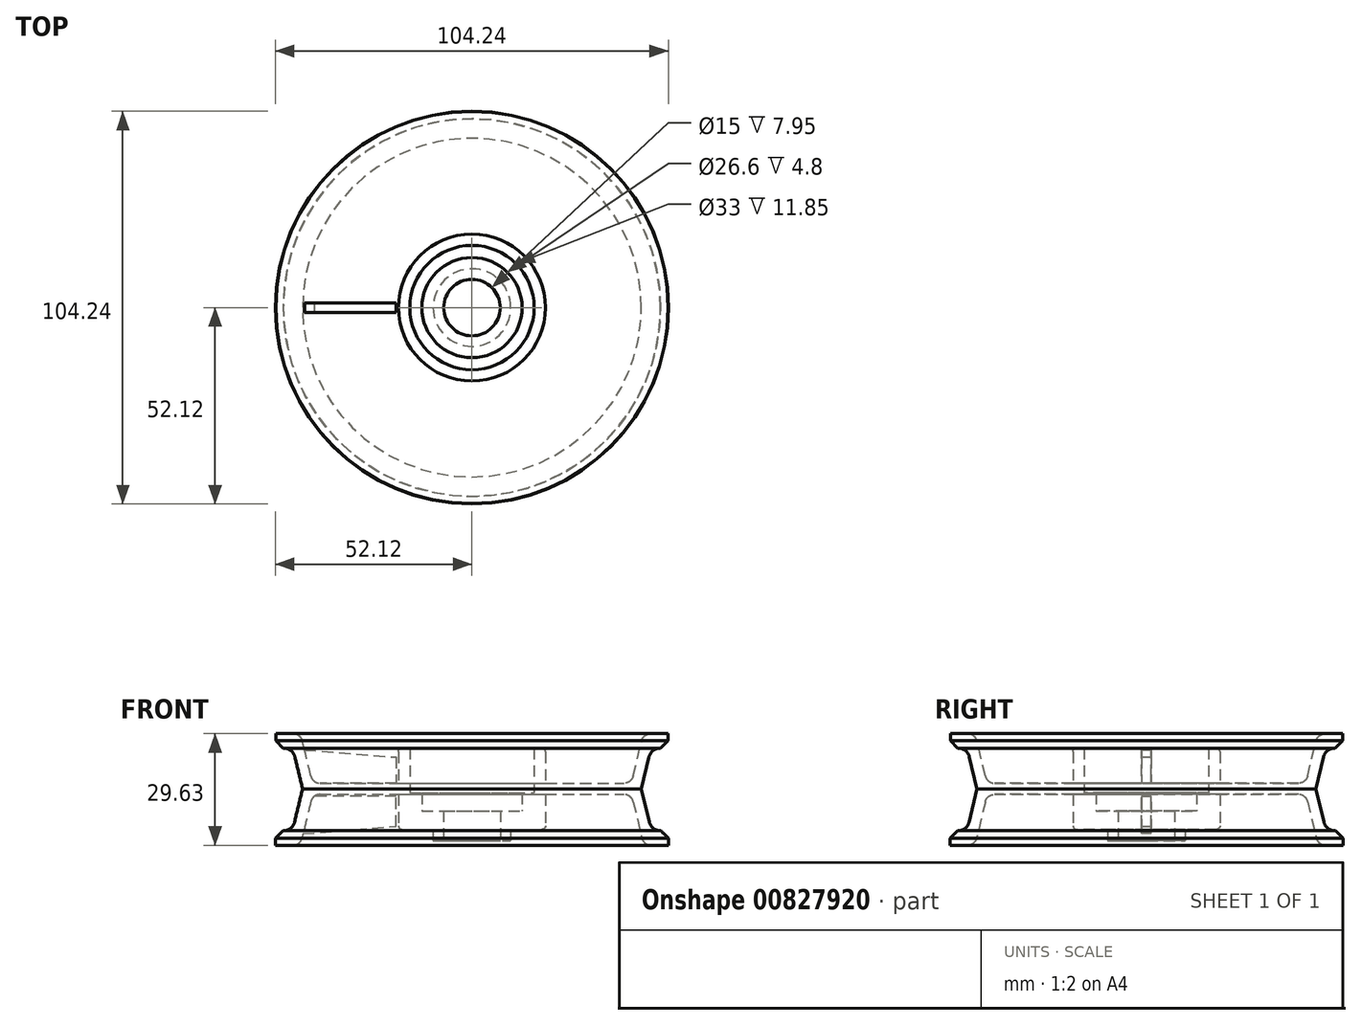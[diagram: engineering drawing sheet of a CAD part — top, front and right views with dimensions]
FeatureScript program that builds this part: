
annotation { "Feature Type Name" : "Feature", "Feature Type Description" : "" }
export const myFeature = defineFeature(function(context is Context, id is Id, definition is map)
    precondition{}
    {
        {
            var Q0;
            Q0=qCreatedBy(makeId("Front.planeOp"),FACE);
            var sketch = newSketch(context, id + "F0", { "sketchPlane" : qUnion([Q0])});
            skLineSegment(sketch, "E0", {"start": v(0, 0) * mm, "end": v(-7.5, 0) * mm, "construction": true});
            skLineSegment(sketch, "E1", {"start": v(-7.5, 0) * mm, "end": v(-10.3, 0) * mm});
            skLineSegment(sketch, "E2.bottom", {"start": v(-10.3, 0) * mm, "end": v(-7.5, 0) * mm});
            skLineSegment(sketch, "E2.top", {"start": v(-10.3, 0) * mm, "end": v(-7.5, 0) * mm});
            skLineSegment(sketch, "E2.left", {"start": v(-10.3, 0) * mm, "end": v(-10.3, 0) * mm});
            skLineSegment(sketch, "E2.right", {"start": v(-7.5, 0) * mm, "end": v(-7.5, 0) * mm});
            skLineSegment(sketch, "E3", {"start": v(-10.3, 0) * mm, "end": v(-10.3, 3) * mm});
            skLineSegment(sketch, "E4", {"start": v(-7.5, 0) * mm, "end": v(-7.5, 7.95) * mm});
            skLineSegment(sketch, "E5", {"start": v(-10.3, 3) * mm, "end": v(-19.5, 3) * mm});
            skLineSegment(sketch, "E6", {"start": v(-7.5, 7.95) * mm, "end": v(-13.3, 7.95) * mm});
            skLineSegment(sketch, "E7", {"start": v(-13.3, 7.95) * mm, "end": v(-13.3, 12.75) * mm});
            skLineSegment(sketch, "E8", {"start": v(-19.5, 3) * mm, "end": v(-19.5, 24.6) * mm});
            skLineSegment(sketch, "E9", {"start": v(-19.5, 24.6) * mm, "end": v(-16.5, 24.6) * mm});
            skLineSegment(sketch, "E10", {"start": v(-16.5, 24.6) * mm, "end": v(-16.5, 12.75) * mm});
            skLineSegment(sketch, "E11", {"start": v(-16.5, 12.75) * mm, "end": v(-13.3, 12.75) * mm});
            skPoint(sketch, "E12", {"position": v(-19.5, 13.8) * mm});
            skLineSegment(sketch, "E13.bottom", {"start": v(-19.5, 15.3) * mm, "end": v(-42.3, 15.3) * mm});
            skLineSegment(sketch, "E13.top", {"start": v(-19.5, 12.3) * mm, "end": v(-42.3, 12.3) * mm});
            skLineSegment(sketch, "E13.left", {"start": v(-19.5, 15.3) * mm, "end": v(-19.5, 12.3) * mm});
            skLineSegment(sketch, "E13.right", {"start": v(-42.3, 15.3) * mm, "end": v(-42.3, 12.3) * mm, "construction": true});
            skLineSegment(sketch, "E14", {"start": v(-42.3, 15.3) * mm, "end": v(-41.94, 13.8) * mm});
            skLineSegment(sketch, "E15", {"start": v(-42.3, 12.3) * mm, "end": v(-41.94, 13.8) * mm});
            skPoint(sketch, "E16", {"position": v(-42.3, 13.8) * mm});
            skPoint(sketch, "E17", {"position": v(-41.94, 13.8) * mm});
            skLineSegment(sketch, "E18", {"start": v(-42.3, 12.3) * mm, "end": v(-45.54, -1.2) * mm});
            skLineSegment(sketch, "E19", {"start": v(-42.3, 15.3) * mm, "end": v(-45.45, 28.43) * mm});
            skLineSegment(sketch, "E20", {"start": v(-41.94, 13.8) * mm, "end": v(-44.94, 13.8) * mm, "construction": true});
            skLineSegment(sketch, "E21", {"start": v(-44.94, 13.8) * mm, "end": v(-48.45, 28.43) * mm});
            skLineSegment(sketch, "E22", {"start": v(-48.45, 28.43) * mm, "end": v(-45.45, 28.43) * mm});
            skLineSegment(sketch, "E23", {"start": v(-44.94, 13.8) * mm, "end": v(-48.54, -1.2) * mm});
            skLineSegment(sketch, "E24", {"start": v(-48.54, -1.2) * mm, "end": v(-45.54, -1.2) * mm});
            skLineSegment(sketch, "E25", {"start": v(-48.45, 28.43) * mm, "end": v(-52.03, 28.43) * mm});
            skLineSegment(sketch, "E26", {"start": v(-52.03, 28.43) * mm, "end": v(-52.03, 24.58) * mm});
            skLineSegment(sketch, "E27", {"start": v(-52.03, 24.58) * mm, "end": v(-47.53, 24.58) * mm});
            skLineSegment(sketch, "E28", {"start": v(-48.54, -1.2) * mm, "end": v(-52.12, -1.2) * mm});
            skLineSegment(sketch, "E29", {"start": v(-52.12, -1.2) * mm, "end": v(-52.12, 2.65) * mm});
            skLineSegment(sketch, "E30", {"start": v(-52.12, 2.65) * mm, "end": v(-47.62, 2.65) * mm});
            skLineSegment(sketch, "E31", {"start": v(0, 0) * mm, "end": v(0, 9.74) * mm, "construction": true});
            skSolve(sketch);
        }
        {
            var Q0;
            Q0=qCreatedBy(makeId("Front.planeOp"),FACE);
            var sketch = newSketch(context, id + "F1", { "sketchPlane" : qUnion([Q0])});
            skLineSegment(sketch, "E32", {"start": v(-45.9, 24.2) * mm, "end": v(-20.1, 22.2) * mm});
            skLineSegment(sketch, "E33", {"start": v(-20.1, 22.2) * mm, "end": v(-20.1, 14.2) * mm});
            skLineSegment(sketch, "E34", {"start": v(-20.1, 14.2) * mm, "end": v(-43.6, 14.2) * mm});
            skLineSegment(sketch, "E35", {"start": v(-43.6, 14.2) * mm, "end": v(-45.9, 24.2) * mm});
            skLineSegment(sketch, "E36", {"start": v(0, 0) * mm, "end": v(0, 30.38) * mm, "construction": true});
            skLineSegment(sketch, "E37", {"start": v(0, 0) * mm, "end": v(-35.46, 0) * mm, "construction": true});
            skLineSegment(sketch, "E38", {"start": v(-43.94, 13) * mm, "end": v(-21.27, 13) * mm, "construction": true});
            skLineSegment(sketch, "E39.MirrorCS", {"start": v(-20.1, 11.8) * mm, "end": v(-43.6, 11.8) * mm});
            skLineSegment(sketch, "E40.MirrorCS", {"start": v(-43.6, 11.8) * mm, "end": v(-45.9, 1.8) * mm});
            skLineSegment(sketch, "E41.MirrorCS", {"start": v(-20.1, 3.8) * mm, "end": v(-20.1, 11.8) * mm});
            skLineSegment(sketch, "E42.MirrorCS", {"start": v(-45.9, 1.8) * mm, "end": v(-20.1, 3.8) * mm});
            skSolve(sketch);
        }
        {
            var Q0;
            Q0 = qSketchRegion(id + "F0", true);
            var Q1;
            Q1=sQuery(id+"F0.wireOp",EDGE,"E31");
            revolve(context, id + "F2", {"surfaceOperationType" : NewSurfaceOperationType.NEW, "entities" : qUnion([Q0]), "axis" : qUnion([Q1]), "revolveType" : RevolveType.FULL});
        }
        {
            var Q0;
            Q0 = qSketchRegion(id + "F1", true);
            extrude(context, id + "F3", {"entities" : qUnion([Q0]), "operationType" : NewBodyOperationType.ADD, "endBound" : BoundingType.SYMMETRIC, "depth" : 2.5 * mm, "offsetDistance" : 25 * mm});
        }
        {
            var Q0;
            Q0=makeQuery(id+"F2.opRevolve","SWEPT_EDGE",EDGE,{"disambiguationData":[OSD([sQuery(id+"F0.wireOp",EDGE,"E19"),sQuery(id+"F0.wireOp",EDGE,"E22")])]});
            var Q1;
            Q1=makeQuery(id+"F2.opRevolve","SWEPT_EDGE",EDGE,{"disambiguationData":[OSD([sQuery(id+"F0.wireOp",EDGE,"E18"),sQuery(id+"F0.wireOp",EDGE,"E24")])]});
            var Q2;
            {var subQ0=sQuery(id+"F0.wireOp",EDGE,"E13.bottom");var subQ1=sQuery(id+"F0.wireOp",EDGE,"E19");var subQ2=sQuery(id+"F1.wireOp",EDGE,"E35");var subQ3=sQuery(id+"F1.wireOp",EDGE,"E34");var subQ4=sQuery(id+"F1.wireOp",EDGE,"E33");var subQ5=sQuery(id+"F1.wireOp",EDGE,"E32");Q2=makeQuery(id+"FbpvuZ5sRYbtWJb_1.1.F3.boolean.opBoolean","SPLIT",EDGE,{"disambiguationData":[TD([makeQuery(id+"F3.opExtrude","CAP_FACE",FACE,{"disambiguationData":[OSD([subQ5,subQ4,subQ3,subQ2])],"isStart":false})])],"derivedFrom":makeQuery(id+"F2.opRevolve","SWEPT_EDGE",EDGE,{"disambiguationData":[OSD([subQ0,sQuery(id+"F0.wireOp",EDGE,"E14"),subQ1])]})});}
            var Q3;
            {var subQ0=sQuery(id+"F0.wireOp",EDGE,"E13.bottom");var subQ2=sQuery(id+"F0.wireOp",EDGE,"E19");var subQ4=sQuery(id+"F1.wireOp",EDGE,"E35");var subQ5=sQuery(id+"F1.wireOp",EDGE,"E34");var subQ6=sQuery(id+"F1.wireOp",EDGE,"E33");var subQ7=sQuery(id+"F1.wireOp",EDGE,"E32");var subQ8=makeQuery(id+"F3.opExtrude","CAP_FACE",FACE,{"disambiguationData":[OSD([subQ7,subQ6,subQ5,subQ4])],"isStart":true});Q3=makeQuery(id+"FbpvuZ5sRYbtWJb_1.5.F3.boolean.opBoolean","SPLIT",EDGE,{"disambiguationData":[TD([subQ8])],"derivedFrom":makeQuery(id+"FbpvuZ5sRYbtWJb_1.4.F3.boolean.opBoolean","SPLIT",EDGE,{"disambiguationData":[TD([subQ8])],"derivedFrom":makeQuery(id+"FbpvuZ5sRYbtWJb_1.3.F3.boolean.opBoolean","SPLIT",EDGE,{"disambiguationData":[TD([subQ8])],"derivedFrom":makeQuery(id+"FbpvuZ5sRYbtWJb_1.2.F3.boolean.opBoolean","SPLIT",EDGE,{"disambiguationData":[TD([subQ8])],"derivedFrom":makeQuery(id+"FbpvuZ5sRYbtWJb_1.1.F3.boolean.opBoolean","SPLIT",EDGE,{"disambiguationData":[TD([subQ8])],"derivedFrom":makeQuery(id+"F2.opRevolve","SWEPT_EDGE",EDGE,{"disambiguationData":[OSD([subQ0,sQuery(id+"F0.wireOp",EDGE,"E14"),subQ2])]})})})})})});}
            var Q4;
            {var subQ0=sQuery(id+"F0.wireOp",EDGE,"E13.bottom");var subQ2=sQuery(id+"F1.wireOp",EDGE,"E35");var subQ3=sQuery(id+"F1.wireOp",EDGE,"E34");var subQ4=sQuery(id+"F1.wireOp",EDGE,"E33");var subQ5=sQuery(id+"F1.wireOp",EDGE,"E32");var subQ6=makeQuery(id+"FbpvuZ5sRYbtWJb_1.4.F3.opExtrude","CAP_FACE",FACE,{"disambiguationData":[OSD([subQ5,subQ4,subQ3,subQ2])],"isStart":false});var subQ7=sQuery(id+"F0.wireOp",EDGE,"E19");var subQ9=makeQuery(id+"F3.opExtrude","CAP_FACE",FACE,{"disambiguationData":[OSD([subQ5,subQ4,subQ3,subQ2])],"isStart":true});Q4=makeQuery(id+"FbpvuZ5sRYbtWJb_1.5.F3.boolean.opBoolean","SPLIT",EDGE,{"disambiguationData":[TD([subQ6])],"derivedFrom":makeQuery(id+"FbpvuZ5sRYbtWJb_1.4.F3.boolean.opBoolean","SPLIT",EDGE,{"disambiguationData":[TD([subQ9])],"derivedFrom":makeQuery(id+"FbpvuZ5sRYbtWJb_1.3.F3.boolean.opBoolean","SPLIT",EDGE,{"disambiguationData":[TD([subQ9])],"derivedFrom":makeQuery(id+"FbpvuZ5sRYbtWJb_1.2.F3.boolean.opBoolean","SPLIT",EDGE,{"disambiguationData":[TD([subQ9])],"derivedFrom":makeQuery(id+"FbpvuZ5sRYbtWJb_1.1.F3.boolean.opBoolean","SPLIT",EDGE,{"disambiguationData":[TD([subQ9])],"derivedFrom":makeQuery(id+"F2.opRevolve","SWEPT_EDGE",EDGE,{"disambiguationData":[OSD([subQ0,sQuery(id+"F0.wireOp",EDGE,"E14"),subQ7])]})})})})})});}
            var Q5;
            {var subQ0=sQuery(id+"F0.wireOp",EDGE,"E13.bottom");var subQ2=sQuery(id+"F0.wireOp",EDGE,"E19");var subQ4=sQuery(id+"F1.wireOp",EDGE,"E35");var subQ5=sQuery(id+"F1.wireOp",EDGE,"E34");var subQ6=sQuery(id+"F1.wireOp",EDGE,"E33");var subQ7=sQuery(id+"F1.wireOp",EDGE,"E32");var subQ8=makeQuery(id+"FbpvuZ5sRYbtWJb_1.3.F3.opExtrude","CAP_FACE",FACE,{"disambiguationData":[OSD([subQ7,subQ6,subQ5,subQ4])],"isStart":false});var subQ9=makeQuery(id+"F3.opExtrude","CAP_FACE",FACE,{"disambiguationData":[OSD([subQ7,subQ6,subQ5,subQ4])],"isStart":true});Q5=makeQuery(id+"FbpvuZ5sRYbtWJb_1.4.F3.boolean.opBoolean","SPLIT",EDGE,{"disambiguationData":[TD([subQ8])],"derivedFrom":makeQuery(id+"FbpvuZ5sRYbtWJb_1.3.F3.boolean.opBoolean","SPLIT",EDGE,{"disambiguationData":[TD([subQ9])],"derivedFrom":makeQuery(id+"FbpvuZ5sRYbtWJb_1.2.F3.boolean.opBoolean","SPLIT",EDGE,{"disambiguationData":[TD([subQ9])],"derivedFrom":makeQuery(id+"FbpvuZ5sRYbtWJb_1.1.F3.boolean.opBoolean","SPLIT",EDGE,{"disambiguationData":[TD([subQ9])],"derivedFrom":makeQuery(id+"F2.opRevolve","SWEPT_EDGE",EDGE,{"disambiguationData":[OSD([subQ0,sQuery(id+"F0.wireOp",EDGE,"E14"),subQ2])]})})})})});}
            var Q6;
            {var subQ0=sQuery(id+"F0.wireOp",EDGE,"E13.bottom");var subQ2=sQuery(id+"F1.wireOp",EDGE,"E35");var subQ3=sQuery(id+"F1.wireOp",EDGE,"E34");var subQ4=sQuery(id+"F1.wireOp",EDGE,"E33");var subQ5=sQuery(id+"F1.wireOp",EDGE,"E32");var subQ6=sQuery(id+"F0.wireOp",EDGE,"E19");var subQ8=makeQuery(id+"FbpvuZ5sRYbtWJb_1.1.F3.opExtrude","CAP_FACE",FACE,{"disambiguationData":[OSD([subQ5,subQ4,subQ3,subQ2])],"isStart":false});Q6=makeQuery(id+"FbpvuZ5sRYbtWJb_1.2.F3.boolean.opBoolean","SPLIT",EDGE,{"disambiguationData":[TD([subQ8])],"derivedFrom":makeQuery(id+"FbpvuZ5sRYbtWJb_1.1.F3.boolean.opBoolean","SPLIT",EDGE,{"disambiguationData":[TD([makeQuery(id+"F3.opExtrude","CAP_FACE",FACE,{"disambiguationData":[OSD([subQ5,subQ4,subQ3,subQ2])],"isStart":true})])],"derivedFrom":makeQuery(id+"F2.opRevolve","SWEPT_EDGE",EDGE,{"disambiguationData":[OSD([subQ0,sQuery(id+"F0.wireOp",EDGE,"E14"),subQ6])]})})});}
            var Q7;
            {var subQ0=sQuery(id+"F0.wireOp",EDGE,"E13.bottom");var subQ2=sQuery(id+"F0.wireOp",EDGE,"E19");var subQ4=sQuery(id+"F1.wireOp",EDGE,"E35");var subQ5=sQuery(id+"F1.wireOp",EDGE,"E34");var subQ6=sQuery(id+"F1.wireOp",EDGE,"E33");var subQ7=sQuery(id+"F1.wireOp",EDGE,"E32");var subQ8=makeQuery(id+"FbpvuZ5sRYbtWJb_1.2.F3.opExtrude","CAP_FACE",FACE,{"disambiguationData":[OSD([subQ7,subQ6,subQ5,subQ4])],"isStart":false});var subQ9=makeQuery(id+"F3.opExtrude","CAP_FACE",FACE,{"disambiguationData":[OSD([subQ7,subQ6,subQ5,subQ4])],"isStart":true});Q7=makeQuery(id+"FbpvuZ5sRYbtWJb_1.3.F3.boolean.opBoolean","SPLIT",EDGE,{"disambiguationData":[TD([subQ8])],"derivedFrom":makeQuery(id+"FbpvuZ5sRYbtWJb_1.2.F3.boolean.opBoolean","SPLIT",EDGE,{"disambiguationData":[TD([subQ9])],"derivedFrom":makeQuery(id+"FbpvuZ5sRYbtWJb_1.1.F3.boolean.opBoolean","SPLIT",EDGE,{"disambiguationData":[TD([subQ9])],"derivedFrom":makeQuery(id+"F2.opRevolve","SWEPT_EDGE",EDGE,{"disambiguationData":[OSD([subQ0,sQuery(id+"F0.wireOp",EDGE,"E14"),subQ2])]})})})});}
            var Q8;
            {var subQ0=sQuery(id+"F0.wireOp",EDGE,"E13.top");var subQ2=sQuery(id+"F1.wireOp",EDGE,"E42.MirrorCS");var subQ3=sQuery(id+"F1.wireOp",EDGE,"E41.MirrorCS");var subQ4=sQuery(id+"F1.wireOp",EDGE,"E40.MirrorCS");var subQ5=sQuery(id+"F1.wireOp",EDGE,"E39.MirrorCS");var subQ6=makeQuery(id+"FbpvuZ5sRYbtWJb_1.4.F3.opExtrude","CAP_FACE",FACE,{"disambiguationData":[OSD([subQ5,subQ4,subQ3,subQ2])],"isStart":false});var subQ7=sQuery(id+"F0.wireOp",EDGE,"E18");var subQ9=makeQuery(id+"F3.opExtrude","CAP_FACE",FACE,{"disambiguationData":[OSD([subQ5,subQ4,subQ3,subQ2])],"isStart":true});Q8=makeQuery(id+"FbpvuZ5sRYbtWJb_1.5.F3.boolean.opBoolean","SPLIT",EDGE,{"disambiguationData":[TD([subQ6])],"derivedFrom":makeQuery(id+"FbpvuZ5sRYbtWJb_1.4.F3.boolean.opBoolean","SPLIT",EDGE,{"disambiguationData":[TD([subQ9])],"derivedFrom":makeQuery(id+"FbpvuZ5sRYbtWJb_1.3.F3.boolean.opBoolean","SPLIT",EDGE,{"disambiguationData":[TD([subQ9])],"derivedFrom":makeQuery(id+"FbpvuZ5sRYbtWJb_1.2.F3.boolean.opBoolean","SPLIT",EDGE,{"disambiguationData":[TD([subQ9])],"derivedFrom":makeQuery(id+"FbpvuZ5sRYbtWJb_1.1.F3.boolean.opBoolean","SPLIT",EDGE,{"disambiguationData":[TD([subQ9])],"derivedFrom":makeQuery(id+"F2.opRevolve","SWEPT_EDGE",EDGE,{"disambiguationData":[OSD([subQ0,sQuery(id+"F0.wireOp",EDGE,"E15"),subQ7])]})})})})})});}
            var Q9;
            {var subQ0=sQuery(id+"F0.wireOp",EDGE,"E13.top");var subQ2=sQuery(id+"F0.wireOp",EDGE,"E18");var subQ4=sQuery(id+"F1.wireOp",EDGE,"E42.MirrorCS");var subQ5=sQuery(id+"F1.wireOp",EDGE,"E41.MirrorCS");var subQ6=sQuery(id+"F1.wireOp",EDGE,"E40.MirrorCS");var subQ7=sQuery(id+"F1.wireOp",EDGE,"E39.MirrorCS");var subQ8=makeQuery(id+"FbpvuZ5sRYbtWJb_1.3.F3.opExtrude","CAP_FACE",FACE,{"disambiguationData":[OSD([subQ7,subQ6,subQ5,subQ4])],"isStart":false});var subQ9=makeQuery(id+"F3.opExtrude","CAP_FACE",FACE,{"disambiguationData":[OSD([subQ7,subQ6,subQ5,subQ4])],"isStart":true});Q9=makeQuery(id+"FbpvuZ5sRYbtWJb_1.4.F3.boolean.opBoolean","SPLIT",EDGE,{"disambiguationData":[TD([subQ8])],"derivedFrom":makeQuery(id+"FbpvuZ5sRYbtWJb_1.3.F3.boolean.opBoolean","SPLIT",EDGE,{"disambiguationData":[TD([subQ9])],"derivedFrom":makeQuery(id+"FbpvuZ5sRYbtWJb_1.2.F3.boolean.opBoolean","SPLIT",EDGE,{"disambiguationData":[TD([subQ9])],"derivedFrom":makeQuery(id+"FbpvuZ5sRYbtWJb_1.1.F3.boolean.opBoolean","SPLIT",EDGE,{"disambiguationData":[TD([subQ9])],"derivedFrom":makeQuery(id+"F2.opRevolve","SWEPT_EDGE",EDGE,{"disambiguationData":[OSD([subQ0,sQuery(id+"F0.wireOp",EDGE,"E15"),subQ2])]})})})})});}
            var Q10;
            {var subQ0=sQuery(id+"F0.wireOp",EDGE,"E13.top");var subQ2=sQuery(id+"F0.wireOp",EDGE,"E18");var subQ4=sQuery(id+"F1.wireOp",EDGE,"E42.MirrorCS");var subQ5=sQuery(id+"F1.wireOp",EDGE,"E41.MirrorCS");var subQ6=sQuery(id+"F1.wireOp",EDGE,"E40.MirrorCS");var subQ7=sQuery(id+"F1.wireOp",EDGE,"E39.MirrorCS");var subQ8=makeQuery(id+"FbpvuZ5sRYbtWJb_1.2.F3.opExtrude","CAP_FACE",FACE,{"disambiguationData":[OSD([subQ7,subQ6,subQ5,subQ4])],"isStart":false});var subQ9=makeQuery(id+"F3.opExtrude","CAP_FACE",FACE,{"disambiguationData":[OSD([subQ7,subQ6,subQ5,subQ4])],"isStart":true});Q10=makeQuery(id+"FbpvuZ5sRYbtWJb_1.3.F3.boolean.opBoolean","SPLIT",EDGE,{"disambiguationData":[TD([subQ8])],"derivedFrom":makeQuery(id+"FbpvuZ5sRYbtWJb_1.2.F3.boolean.opBoolean","SPLIT",EDGE,{"disambiguationData":[TD([subQ9])],"derivedFrom":makeQuery(id+"FbpvuZ5sRYbtWJb_1.1.F3.boolean.opBoolean","SPLIT",EDGE,{"disambiguationData":[TD([subQ9])],"derivedFrom":makeQuery(id+"F2.opRevolve","SWEPT_EDGE",EDGE,{"disambiguationData":[OSD([subQ0,sQuery(id+"F0.wireOp",EDGE,"E15"),subQ2])]})})})});}
            var Q11;
            {var subQ0=sQuery(id+"F0.wireOp",EDGE,"E13.top");var subQ2=sQuery(id+"F1.wireOp",EDGE,"E42.MirrorCS");var subQ3=sQuery(id+"F1.wireOp",EDGE,"E41.MirrorCS");var subQ4=sQuery(id+"F1.wireOp",EDGE,"E40.MirrorCS");var subQ5=sQuery(id+"F1.wireOp",EDGE,"E39.MirrorCS");var subQ6=sQuery(id+"F0.wireOp",EDGE,"E18");var subQ8=makeQuery(id+"FbpvuZ5sRYbtWJb_1.1.F3.opExtrude","CAP_FACE",FACE,{"disambiguationData":[OSD([subQ5,subQ4,subQ3,subQ2])],"isStart":false});Q11=makeQuery(id+"FbpvuZ5sRYbtWJb_1.2.F3.boolean.opBoolean","SPLIT",EDGE,{"disambiguationData":[TD([subQ8])],"derivedFrom":makeQuery(id+"FbpvuZ5sRYbtWJb_1.1.F3.boolean.opBoolean","SPLIT",EDGE,{"disambiguationData":[TD([makeQuery(id+"F3.opExtrude","CAP_FACE",FACE,{"disambiguationData":[OSD([subQ5,subQ4,subQ3,subQ2])],"isStart":true})])],"derivedFrom":makeQuery(id+"F2.opRevolve","SWEPT_EDGE",EDGE,{"disambiguationData":[OSD([subQ0,sQuery(id+"F0.wireOp",EDGE,"E15"),subQ6])]})})});}
            var Q12;
            {var subQ0=sQuery(id+"F0.wireOp",EDGE,"E13.top");var subQ1=sQuery(id+"F0.wireOp",EDGE,"E18");var subQ2=sQuery(id+"F1.wireOp",EDGE,"E42.MirrorCS");var subQ3=sQuery(id+"F1.wireOp",EDGE,"E41.MirrorCS");var subQ4=sQuery(id+"F1.wireOp",EDGE,"E40.MirrorCS");var subQ5=sQuery(id+"F1.wireOp",EDGE,"E39.MirrorCS");Q12=makeQuery(id+"FbpvuZ5sRYbtWJb_1.1.F3.boolean.opBoolean","SPLIT",EDGE,{"disambiguationData":[TD([makeQuery(id+"F3.opExtrude","CAP_FACE",FACE,{"disambiguationData":[OSD([subQ5,subQ4,subQ3,subQ2])],"isStart":false})])],"derivedFrom":makeQuery(id+"F2.opRevolve","SWEPT_EDGE",EDGE,{"disambiguationData":[OSD([subQ0,sQuery(id+"F0.wireOp",EDGE,"E15"),subQ1])]})});}
            var Q13;
            {var subQ0=sQuery(id+"F0.wireOp",EDGE,"E13.top");var subQ2=sQuery(id+"F0.wireOp",EDGE,"E18");var subQ4=sQuery(id+"F1.wireOp",EDGE,"E42.MirrorCS");var subQ5=sQuery(id+"F1.wireOp",EDGE,"E41.MirrorCS");var subQ6=sQuery(id+"F1.wireOp",EDGE,"E40.MirrorCS");var subQ7=sQuery(id+"F1.wireOp",EDGE,"E39.MirrorCS");var subQ8=makeQuery(id+"F3.opExtrude","CAP_FACE",FACE,{"disambiguationData":[OSD([subQ7,subQ6,subQ5,subQ4])],"isStart":true});Q13=makeQuery(id+"FbpvuZ5sRYbtWJb_1.5.F3.boolean.opBoolean","SPLIT",EDGE,{"disambiguationData":[TD([subQ8])],"derivedFrom":makeQuery(id+"FbpvuZ5sRYbtWJb_1.4.F3.boolean.opBoolean","SPLIT",EDGE,{"disambiguationData":[TD([subQ8])],"derivedFrom":makeQuery(id+"FbpvuZ5sRYbtWJb_1.3.F3.boolean.opBoolean","SPLIT",EDGE,{"disambiguationData":[TD([subQ8])],"derivedFrom":makeQuery(id+"FbpvuZ5sRYbtWJb_1.2.F3.boolean.opBoolean","SPLIT",EDGE,{"disambiguationData":[TD([subQ8])],"derivedFrom":makeQuery(id+"FbpvuZ5sRYbtWJb_1.1.F3.boolean.opBoolean","SPLIT",EDGE,{"disambiguationData":[TD([subQ8])],"derivedFrom":makeQuery(id+"F2.opRevolve","SWEPT_EDGE",EDGE,{"disambiguationData":[OSD([subQ0,sQuery(id+"F0.wireOp",EDGE,"E15"),subQ2])]})})})})})});}
            fillet(context, id + "F4", {"entities" : qUnion([Q0, Q1, Q2, Q3, Q4, Q5, Q6, Q7, Q8, Q9, Q10, Q11, Q12, Q13]), "radius" : 2.5 * mm, "tangentPropagation" : true, "allowEdgeOverflow" : false});
        }
        {
            var Q0;
            Q0=makeQuery(id+"F2.opRevolve","SWEPT_EDGE",EDGE,{"disambiguationData":[OSD([sQuery(id+"F0.wireOp",EDGE,"E8"),sQuery(id+"F0.wireOp",EDGE,"E9")])]});
            var Q1;
            Q1=makeQuery(id+"F2.opRevolve","SWEPT_EDGE",EDGE,{"disambiguationData":[OSD([sQuery(id+"F0.wireOp",EDGE,"E5"),sQuery(id+"F0.wireOp",EDGE,"E8")])]});
            fillet(context, id + "F5", {"entities" : qUnion([Q0, Q1]), "radius" : 1 * mm, "tangentPropagation" : true, "allowEdgeOverflow" : false});
        }
        {
            var Q0;
            Q0=makeQuery(id+"F2.opRevolve","SWEPT_EDGE",EDGE,{"disambiguationData":[OSD([sQuery(id+"F0.wireOp",EDGE,"E26"),sQuery(id+"F0.wireOp",EDGE,"E27")])]});
            var Q1;
            Q1=makeQuery(id+"F2.opRevolve","SWEPT_EDGE",EDGE,{"disambiguationData":[OSD([sQuery(id+"F0.wireOp",EDGE,"E29"),sQuery(id+"F0.wireOp",EDGE,"E30")])]});
            chamfer(context, id + "F6", {"entities" : qUnion([Q0, Q1]), "width" : 2 * mm, "tangentPropagation" : true});
        }
        {
            var Q0;
            Q0=makeQuery(id+"F2.opRevolve","SWEPT_EDGE",EDGE,{"disambiguationData":[OSD([sQuery(id+"F0.wireOp",EDGE,"E21"),sQuery(id+"F0.wireOp",EDGE,"E27")])]});
            var Q1;
            Q1=makeQuery(id+"F2.opRevolve","SWEPT_EDGE",EDGE,{"disambiguationData":[OSD([sQuery(id+"F0.wireOp",EDGE,"E23"),sQuery(id+"F0.wireOp",EDGE,"E30")])]});
            fillet(context, id + "F7", {"entities" : qUnion([Q0, Q1]), "radius" : 3 * mm, "tangentPropagation" : true, "allowEdgeOverflow" : false});
        }
    });
